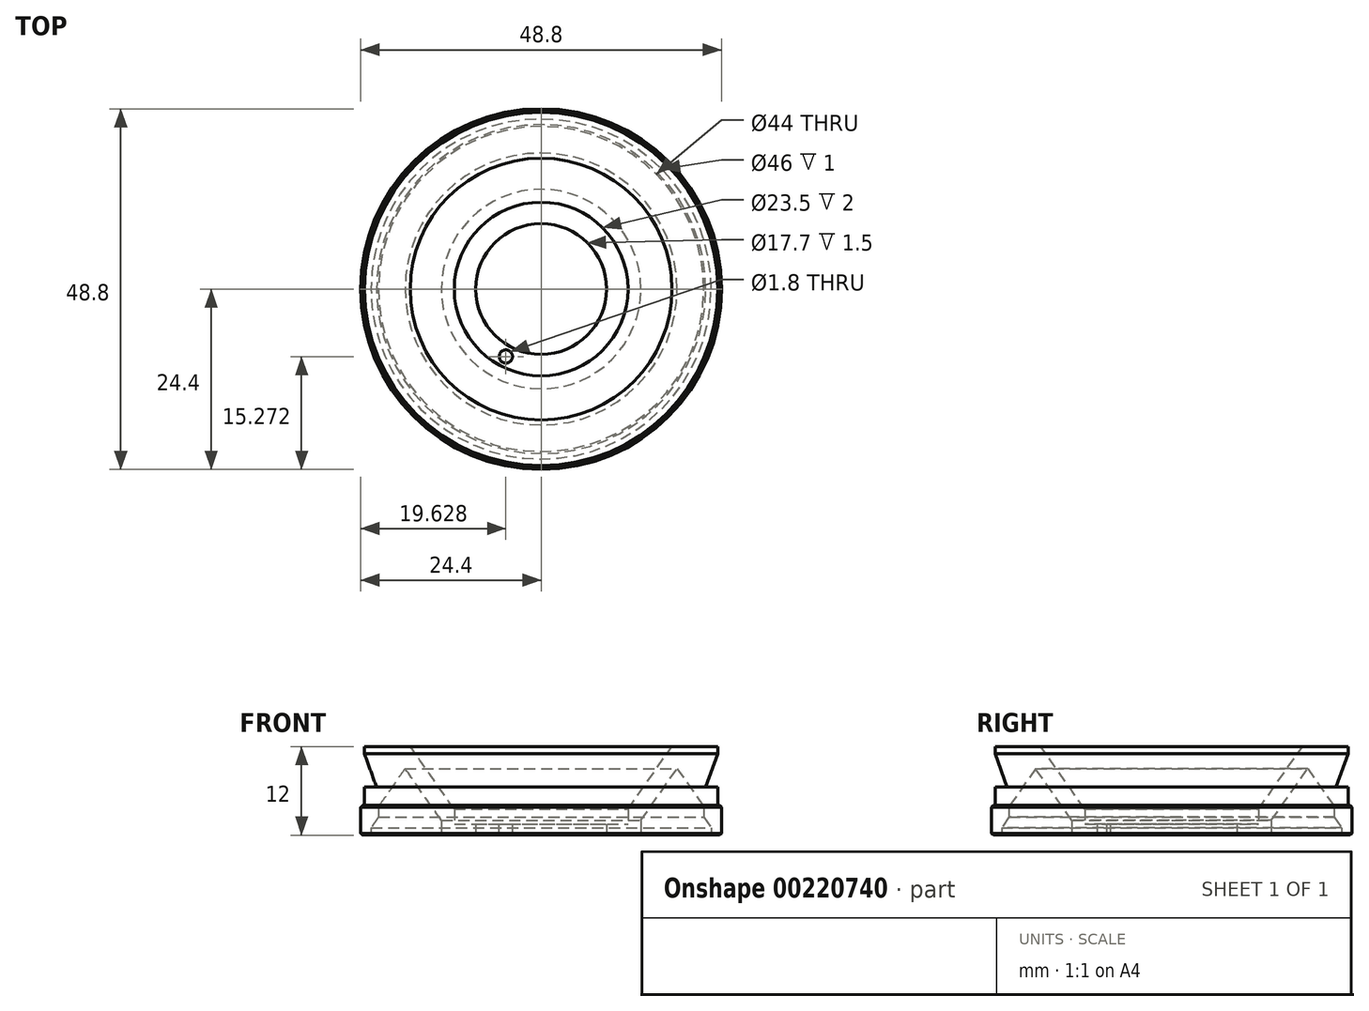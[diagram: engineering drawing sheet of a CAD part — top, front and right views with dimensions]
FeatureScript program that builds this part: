
annotation { "Feature Type Name" : "Feature", "Feature Type Description" : "" }
export const myFeature = defineFeature(function(context is Context, id is Id, definition is map)
    precondition{}
    {
        {
            var Q0;
            Q0=qCreatedBy(makeId("Front.planeOp"),FACE);
            var sketch = newSketch(context, id + "F0", { "sketchPlane" : qUnion([Q0])});
            skLineSegment(sketch, "E0", {"start": v(17.7, 1.22) * mm, "end": v(23.9, 1.22) * mm});
            skLineSegment(sketch, "E1", {"start": v(23.9, 1.22) * mm, "end": v(23.9, 0.22) * mm});
            skLineSegment(sketch, "E2", {"start": v(23.9, 0.22) * mm, "end": v(22.26, -4.28) * mm});
            skLineSegment(sketch, "E3", {"start": v(22.26, -4.28) * mm, "end": v(23.9, -4.28) * mm});
            skLineSegment(sketch, "E4", {"start": v(23.9, -4.28) * mm, "end": v(23.9, -4.28) * mm});
            skLineSegment(sketch, "E5", {"start": v(24.4, -7.03) * mm, "end": v(24.4, -10.53) * mm});
            skLineSegment(sketch, "E6", {"start": v(22, -8.35) * mm, "end": v(22, -6.92) * mm});
            skLineSegment(sketch, "E7", {"start": v(13.5, -8.78) * mm, "end": v(13.5, -10.78) * mm});
            skLineSegment(sketch, "E8", {"start": v(13.5, -10.78) * mm, "end": v(8.85, -10.78) * mm});
            skLineSegment(sketch, "E9", {"start": v(8.85, -10.78) * mm, "end": v(8.85, -9.28) * mm});
            skLineSegment(sketch, "E10", {"start": v(8.85, -9.28) * mm, "end": v(11.75, -9.28) * mm});
            skLineSegment(sketch, "E11", {"start": v(11.75, -9.28) * mm, "end": v(11.75, -7.28) * mm});
            skLineSegment(sketch, "E12", {"start": v(11.75, -7.28) * mm, "end": v(17.7, 1.22) * mm});
            skLineSegment(sketch, "E13", {"start": v(24.15, -10.78) * mm, "end": v(23, -10.78) * mm});
            skLineSegment(sketch, "E14", {"start": v(23, -10.78) * mm, "end": v(23, -9.78) * mm});
            skLineSegment(sketch, "E15", {"start": v(23, -9.78) * mm, "end": v(22, -8.35) * mm});
            skLineSegment(sketch, "E16", {"start": v(13.5, -8.78) * mm, "end": v(18.4, -1.78) * mm});
            skLineSegment(sketch, "E17", {"start": v(18.4, -1.78) * mm, "end": v(22, -6.92) * mm});
            skLineSegment(sketch, "E18", {"start": v(23.9, -4.28) * mm, "end": v(23.9, -6.78) * mm});
            skLineSegment(sketch, "E19", {"start": v(23.9, -6.78) * mm, "end": v(24.15, -6.78) * mm});
            skLineSegment(sketch, "E20", {"start": v(24.15, -6.78) * mm, "end": v(24.4, -7.03) * mm});
            skLineSegment(sketch, "E21", {"start": v(24.4, -10.53) * mm, "end": v(24.15, -10.78) * mm});
            skSolve(sketch);
        }
        {
            var Q0;
            Q0=qCreatedBy(makeId("Front.planeOp"),FACE);
            var sketch = newSketch(context, id + "F1", { "sketchPlane" : qUnion([Q0])});
            skLineSegment(sketch, "E22", {"start": v(0, 0) * mm, "end": v(0, 37.5) * mm});
            skSolve(sketch);
        }
        {
            var Q0;
            Q0=makeQuery(id+"F0.imprint","IMPRINT",FACE,{"disambiguationData":[TD([[makeQuery(id+"F0.imprint","IMPRINT",EDGE,{"derivedFrom":sQuery(id+"F0.wireOp",EDGE,"E0")}),-1.0]])]});
            var Q1;
            Q1=sQuery(id+"F1.wireOp",EDGE,"E22");
            revolve(context, id + "F2", {"entities" : qUnion([Q0]), "axis" : qUnion([Q1]), "revolveType" : RevolveType.FULL});
        }
        {
            var Q0;
            Q0=makeQuery(id+"F2.opRevolve","SWEPT_FACE",FACE,{"disambiguationData":[OSD([sQuery(id+"F0.wireOp",EDGE,"E8")])]});
            var sketch = newSketch(context, id + "F3", { "sketchPlane" : qUnion([Q0])});
            skCircle(sketch, "E23", {"center": v(0, 0) * mm, "radius": 10.3 * mm, "construction": true});
            skPoint(sketch, "E24", {"position": v(-4.77, 9.13) * mm});
            skSolve(sketch);
        }
        {
            var Q0;
            Q0=sQuery(id+"F3.wireOp",VERTEX,"E24");
            var Q1;
            Q1=makeQuery(id+"F2.opRevolve","SWEPT_BODY",BODY,{"disambiguationData":[OSD([sQuery(id+"F0.wireOp",EDGE,"E0"),sQuery(id+"F0.wireOp",EDGE,"E1"),sQuery(id+"F0.wireOp",EDGE,"E2"),sQuery(id+"F0.wireOp",EDGE,"E3"),sQuery(id+"F0.wireOp",EDGE,"E4"),sQuery(id+"F0.wireOp",EDGE,"iEqigx3r-xVGF-031j-RGFS-d7iRF83fJ3bl"),sQuery(id+"F0.wireOp",EDGE,"E5"),sQuery(id+"F0.wireOp",EDGE,"fayYD0gm-lNcB-B1eb-2VQN-oCw3MGGlbdqD"),sQuery(id+"F0.wireOp",EDGE,"E6"),sQuery(id+"F0.wireOp",EDGE,"6VdWqs0S-yfu5-WLMF-cnbi-b0Se1CMhXnd5"),sQuery(id+"F0.wireOp",EDGE,"E7"),sQuery(id+"F0.wireOp",EDGE,"E8"),sQuery(id+"F0.wireOp",EDGE,"E9"),sQuery(id+"F0.wireOp",EDGE,"yOFk7YBI-3UHL-WxcC-XtCi-ltcMaYCbp533"),sQuery(id+"F0.wireOp",EDGE,"LYuHrEQR-UMly-UtHU-eEpl-ZHuv2FlVC1YU"),sQuery(id+"F0.wireOp",EDGE,"E10"),sQuery(id+"F0.wireOp",EDGE,"E11"),sQuery(id+"F0.wireOp",EDGE,"E12")])]});
            hole(context, id + "F4", {"style" : HoleStyle.SIMPLE, "endStyle" : HoleEndStyle.THROUGH, "holeDiameter" : 1.8 * mm, "locations" : qUnion([Q0]), "scope" : qUnion([Q1]), "isTappedThrough" : true, "startStyle" : HoleStartStyle.PART});
        }
    });
